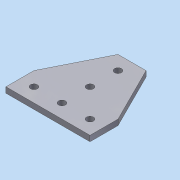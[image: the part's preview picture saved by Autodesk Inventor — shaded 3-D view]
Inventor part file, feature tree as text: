
AUTODESK INVENTOR PART (.ipt)
format: ipt  version: 2013 (Build 170138000, 138)  size: 97,280 bytes
history: native  units: mm
features: sketch x2, extrude x1, hole x1
ambient origin geometry x8: Origin, YZ Plane, XZ Plane, XY Plane, X Axis, Y Axis, Z Axis, Center Point
bodies: Solid1 (feature_tree)
feature tree (4):
  extrude  "Extrusion1"  Depth=20.0mm
  hole  "Hole1"  [1 undecoded]
  sketch  "Sketch1"  dims[d0=20.0mm d2=20.0mm]
  sketch  "Sketch2"  dims[d3=60.0mm d4=60.0mm d5=4.0mm d6=0.0mm d7=40.0mm d9=20.0mm d10=20.0mm d11=20.0mm d12=5.0mm d13=6.0mm d14=4.0mm d15=2.0mm d16=90.0deg d17=8.0mm d18=20.594885mm]
note: 1 required parameter value undecoded (feature->parameter linkage not recoverable at this tier; creation-order binding heuristic only, values carry confidence <= 0.55)
